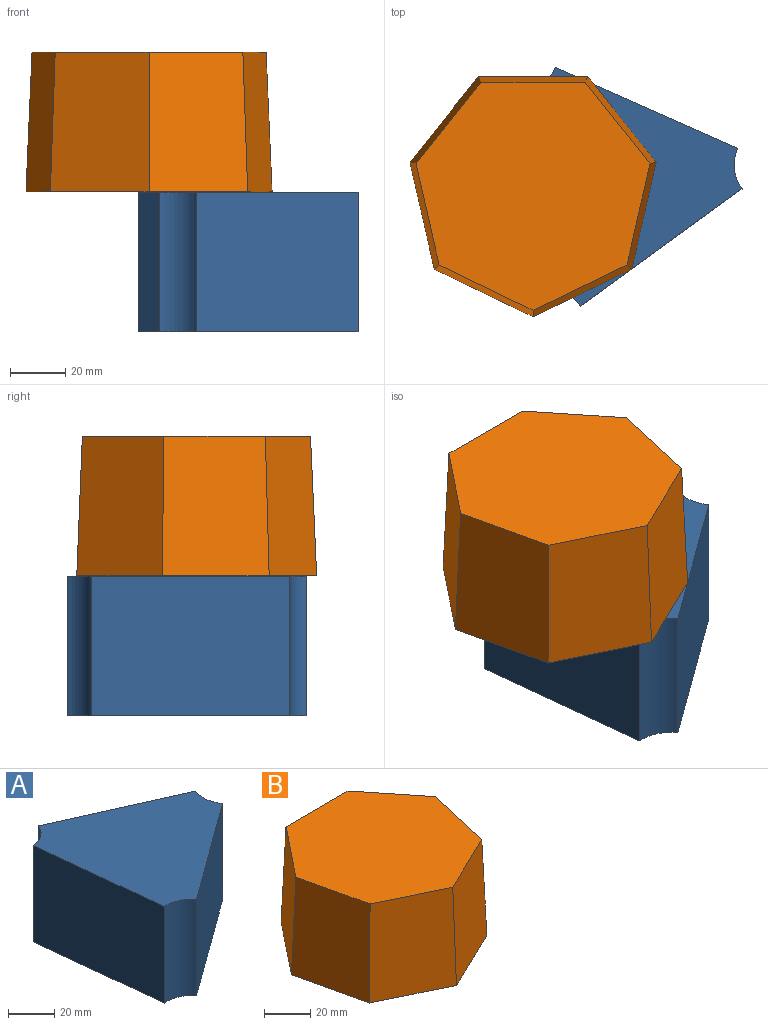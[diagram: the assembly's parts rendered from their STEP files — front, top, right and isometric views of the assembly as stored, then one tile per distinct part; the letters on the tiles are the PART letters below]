
ASSEMBLY  parts=2 mates=1
PART A: 8 faces, bbox 79.7x86.7x50.8 mm
  f0: plane 58.55x50.8mm, normal (0.59,-0.81,0), area 3679mm2, adj f1,f5,f6,f7
  f1: cylinder r=14.82mm len=50.8mm, axis (0,0,-1), area 788.2mm2, adj f0,f2,f6,f7
  f2: plane 66.19x50.8mm, normal (0.41,0.91,0), area 3679mm2, adj f1,f3,f6,f7
  f3: cylinder r=14.82mm len=50.8mm, axis (0,0,-1), area 788.2mm2, adj f2,f4,f6,f7
  f4: plane 72.02x50.8mm, normal (-0.99,-0.11,0), area 3679mm2, adj f3,f5,f6,f7
  f5: cylinder r=14.82mm len=50.8mm, axis (0,0,-1), area 788.2mm2, adj f0,f4,f6,f7
  f6: plane 86.75x79.73mm, normal (0,0,1), area 4164.9mm2, adj f0,f1,f2,f3,f4,f5
  f7: plane 86.75x79.73mm, normal (0,0,-1), area 4164.9mm2, adj f0,f1,f2,f3,f4,f5
PART B: 9 faces, bbox 89.4x87.1x50.8 mm
  f0: plane 85.02x82.89mm, normal (0,0,1), area 5202.7mm2, adj f2,f3,f4,f5,f6,f7,f8
  f1: plane 89.38x87.14mm, normal (0,0,-1), area 5750mm2, adj f2,f3,f4,f5,f6,f7,f8
  f2: plane 50.8x39.78mm, normal (0,1,0.04), area 1973mm2, adj f0,f1,f3,f8
  f3: plane 50.8x31.6mm, normal (0.78,0.62,0.04), area 1973mm2, adj f0,f1,f2,f4
  f4: plane 50.8x38.78mm, normal (0.97,-0.22,0.04), area 1973mm2, adj f0,f1,f3,f5
  f5: plane 50.8x35.84mm, normal (0.43,-0.9,0.04), area 1973mm2, adj f0,f1,f4,f6
  f6: plane 50.8x35.84mm, normal (-0.43,-0.9,0.04), area 1973mm2, adj f0,f1,f5,f7
  f7: plane 50.8x38.78mm, normal (-0.97,-0.22,0.04), area 1973mm2, adj f0,f1,f6,f8
  f8: plane 50.8x31.6mm, normal (-0.78,0.62,0.04), area 1973mm2, adj f0,f1,f2,f7
PLACE A t=(25.3,12.26,-62.42)mm
PLACE B t=(-3.99,9.15,-11.62)mm
MATE fastened A.f6 <-> B.f1  axis (0,0,1) through (-3.99,9.15,-11.62)mm
